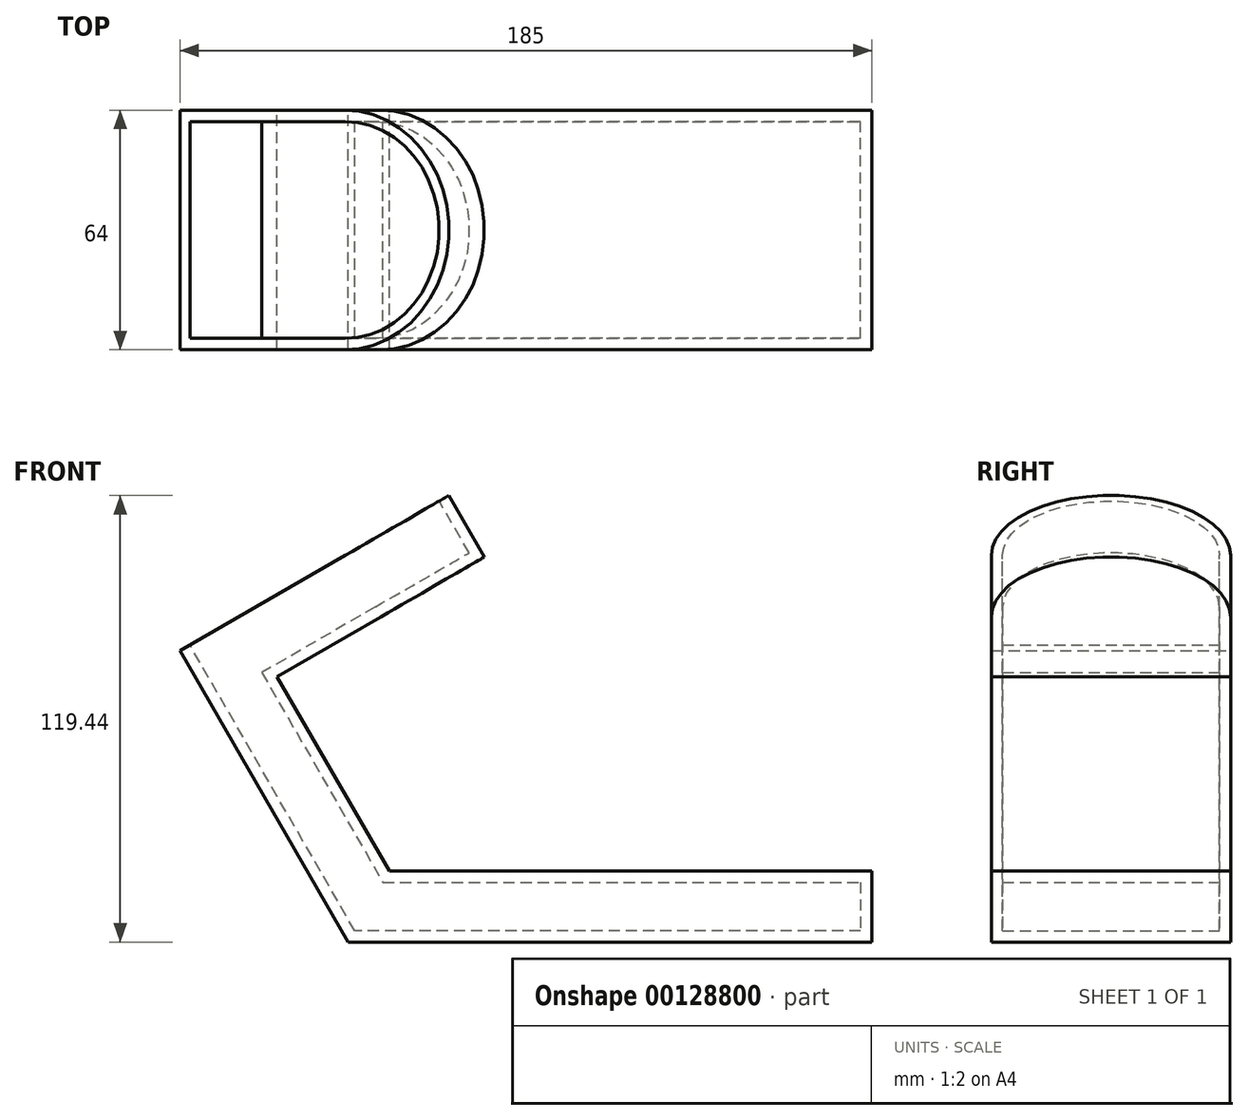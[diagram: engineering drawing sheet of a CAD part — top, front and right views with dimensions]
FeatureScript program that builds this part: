
annotation { "Feature Type Name" : "Feature", "Feature Type Description" : "" }
export const myFeature = defineFeature(function(context is Context, id is Id, definition is map)
    precondition{}
    {
        {
            var Q0;
            Q0=qCreatedBy(makeId("Front.planeOp"),FACE);
            var sketch = newSketch(context, id + "F0", { "sketchPlane" : qUnion([Q0])});
            skLineSegment(sketch, "E0", {"start": v(80.98, -38.64) * mm, "end": v(-59.02, -38.64) * mm});
            skLineSegment(sketch, "E1", {"start": v(-59.02, -38.64) * mm, "end": v(-104.02, 39.3) * mm});
            skLineSegment(sketch, "E2", {"start": v(-104.02, 39.3) * mm, "end": v(-59.85, 64.8) * mm});
            skLineSegment(sketch, "E3", {"start": v(-59.85, 64.8) * mm, "end": v(-50.35, 48.34) * mm});
            skLineSegment(sketch, "E4", {"start": v(-50.35, 48.34) * mm, "end": v(-78.07, 32.34) * mm});
            skLineSegment(sketch, "E5", {"start": v(-78.07, 32.34) * mm, "end": v(-48.05, -19.64) * mm});
            skLineSegment(sketch, "E6", {"start": v(-48.05, -19.64) * mm, "end": v(80.98, -19.64) * mm});
            skLineSegment(sketch, "E7", {"start": v(80.98, -19.64) * mm, "end": v(80.98, -38.64) * mm});
            skSolve(sketch);
        }
        {
            var Q0;
            Q0=makeQuery(id+"F0.imprint","IMPRINT",FACE,{"disambiguationData":[TD([[makeQuery(id+"F0.imprint","IMPRINT",EDGE,{"derivedFrom":sQuery(id+"F0.wireOp",EDGE,"E0")}),-1.0]])]});
            extrude(context, id + "F1", {"entities" : qUnion([Q0]), "depth" : 64 * mm});
        }
        {
            var Q0;
            Q0=makeQuery(id+"F1.opExtrude","SWEPT_FACE",FACE,{"disambiguationData":[OSD([sQuery(id+"F0.wireOp",EDGE,"E2")])]});
            var sketch = newSketch(context, id + "F2", { "sketchPlane" : qUnion([Q0])});
            skCircle(sketch, "E8", {"center": v(-19.43, -32) * mm, "radius": 32 * mm});
            skSolve(sketch);
        }
        {
            var Q0;
            {var subQ1=sQuery(id+"F0.wireOp",EDGE,"E2");var subQ2=makeQuery(id+"F1.opExtrude","SWEPT_EDGE",EDGE,{"disambiguationData":[OSD([subQ1,sQuery(id+"F0.wireOp",EDGE,"E3")])]});Q0=makeQuery(id+"F2.imprint","IMPRINT",FACE,{"disambiguationData":[TD([[makeQuery(id+"F2.imprint","IMPRINT",EDGE,{"derivedFrom":subQ2}),-1.0]])]});}
            extrude(context, id + "F3", {"entities" : qUnion([Q0]), "operationType" : NewBodyOperationType.ADD, "oppositeDirection" : true, "depth" : 19 * mm});
        }
        {
            var Q0;
            {var subQ0=sQuery(id+"F0.wireOp",EDGE,"E2");Q0=makeQuery(id+"F3.boolean.opBoolean","MERGE",FACE,{"derivedFrom":[makeQuery(id+"F1.opExtrude","SWEPT_FACE",FACE,{"disambiguationData":[OSD([subQ0])]}),makeQuery(id+"F3.opExtrude","CAP_FACE",FACE,{"disambiguationData":[OSD([subQ0,sQuery(id+"F0.wireOp",EDGE,"E3"),sQuery(id+"F2.wireOp",EDGE,"E8")])],"isStart":true})]});}
            shell(context, id + "F4", {"entities" : qUnion([Q0]), "thickness" : 3 * mm});
        }
        {
            var Q0;
            Q0=makeQuery(id+"F4.opShell","OFFSET_FACE",FACE,{"disambiguationData":[OSD([sQuery(id+"F0.wireOp",EDGE,"E2"),sQuery(id+"F0.wireOp",EDGE,"E3"),sQuery(id+"F0.wireOp",EDGE,"E4"),sQuery(id+"F2.wireOp",EDGE,"E8")])]});
            var sketch = newSketch(context, id + "F5", { "sketchPlane" : qUnion([Q0])});
            skCircle(sketch, "E9", {"center": v(-19.43, -32) * mm, "radius": 9.5 * mm});
            skSolve(sketch);
        }
        {
            var Q0;
            Q0=makeQuery(id+"F5.imprint","IMPRINT",FACE,{"disambiguationData":[TD([[makeQuery(id+"F5.imprint","IMPRINT",EDGE,{"derivedFrom":sQuery(id+"F5.wireOp",EDGE,"E9")}),1.0]])]});
            extrude(context, id + "F6", {"entities" : qUnion([Q0]), "operationType" : NewBodyOperationType.ADD, "oppositeDirection" : true, "depth" : 3 * mm});
        }
    });
